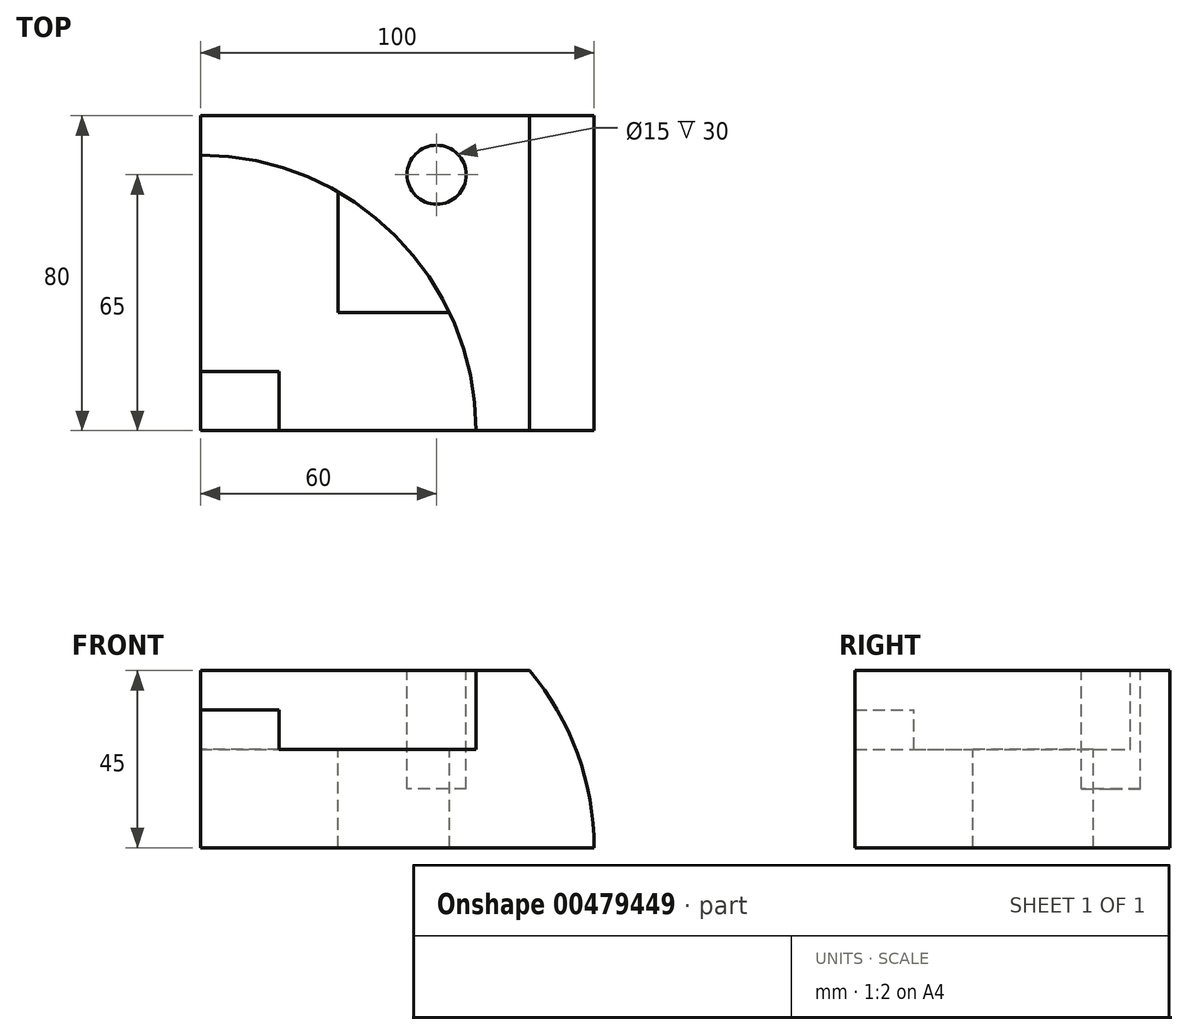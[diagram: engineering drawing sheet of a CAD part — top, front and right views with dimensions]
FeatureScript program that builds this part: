
annotation { "Feature Type Name" : "Feature", "Feature Type Description" : "" }
export const myFeature = defineFeature(function(context is Context, id is Id, definition is map)
    precondition{}
    {
        {
            var Q0;
            Q0=qCreatedBy(makeId("Top.planeOp"),FACE);
            var sketch = newSketch(context, id + "F0", { "sketchPlane" : qUnion([Q0])});
            skLineSegment(sketch, "E0.bottom", {"start": v(0, 0) * mm, "end": v(100, 0) * mm});
            skLineSegment(sketch, "E0.top", {"start": v(0, 80) * mm, "end": v(100, 80) * mm});
            skLineSegment(sketch, "E0.left", {"start": v(0, 0) * mm, "end": v(0, 80) * mm});
            skLineSegment(sketch, "E0.right", {"start": v(100, 0) * mm, "end": v(100, 80) * mm});
            skSolve(sketch);
        }
        {
            var Q0;
            Q0 = qSketchRegion(id + "F0", true);
            extrude(context, id + "F1", {"entities" : qUnion([Q0]), "depth" : 45 * mm});
        }
        {
            var Q0;
            Q0=makeQuery(id+"F1.opExtrude","SWEPT_FACE",FACE,{"disambiguationData":[OSD([sQuery(id+"F0.wireOp",EDGE,"E0.bottom")])]});
            var sketch = newSketch(context, id + "F2", { "sketchPlane" : qUnion([Q0])});
            skLineSegment(sketch, "E1", {"start": v(100, 45) * mm, "end": v(100, 0) * mm});
            skArc(sketch, "E2", {"start": v(100, 0) * mm, "mid": v(95.78, 23.94) * mm, "end": v(83.62, 45) * mm});
            skLineSegment(sketch, "E3", {"start": v(83.62, 45) * mm, "end": v(100, 45) * mm});
            skSolve(sketch);
        }
        {
            var Q0;
            Q0=makeQuery(id+"F2.imprint","IMPRINT",FACE,{"disambiguationData":[TD([[makeQuery(id+"F2.imprint","IMPRINT",EDGE,{"derivedFrom":sQuery(id+"F2.wireOp",EDGE,"E1")}),-1.0]])]});
            extrude(context, id + "F3", {"entities" : qUnion([Q0]), "operationType" : NewBodyOperationType.REMOVE, "endBound" : BoundingType.THROUGH_ALL, "oppositeDirection" : true, "depth" : 25 * mm});
        }
        {
            var Q0;
            Q0=makeQuery(id+"F1.opExtrude","CAP_FACE",FACE,{"disambiguationData":[OSD([sQuery(id+"F0.wireOp",EDGE,"E0.bottom"),sQuery(id+"F0.wireOp",EDGE,"E0.top"),sQuery(id+"F0.wireOp",EDGE,"E0.left"),sQuery(id+"F0.wireOp",EDGE,"E0.right")])],"isStart":false});
            var sketch = newSketch(context, id + "F4", { "sketchPlane" : qUnion([Q0])});
            skArc(sketch, "E4", {"start": v(70, 0) * mm, "mid": v(49.5, 49.5) * mm, "end": v(0, 70) * mm});
            skLineSegment(sketch, "E5.bottom", {"start": v(0, 0) * mm, "end": v(20, 0) * mm});
            skLineSegment(sketch, "E5.top", {"start": v(0, 15) * mm, "end": v(20, 15) * mm});
            skLineSegment(sketch, "E5.left", {"start": v(0, 0) * mm, "end": v(0, 15) * mm});
            skLineSegment(sketch, "E5.right", {"start": v(20, 0) * mm, "end": v(20, 15) * mm});
            skSolve(sketch);
        }
        {
            var Q0;
            {var subQ0=sQuery(id+"F4.wireOp",EDGE,"E4");Q0=makeQuery(id+"F4.imprint","IMPRINT",FACE,{"disambiguationData":[TD([[makeQuery(id+"F4.imprint","IMPRINT",EDGE,{"derivedFrom":subQ0}),1.0]])]});}
            extrude(context, id + "F5", {"entities" : qUnion([Q0]), "operationType" : NewBodyOperationType.REMOVE, "oppositeDirection" : true, "depth" : 20 * mm});
        }
        {
            var Q0;
            {var subQ0=sQuery(id+"F0.wireOp",EDGE,"E0.bottom");var subQ1=sQuery(id+"F0.wireOp",EDGE,"E0.left");Q0=makeQuery(id+"F5.boolean.opBoolean","SPLIT",FACE,{"disambiguationData":[TD([makeQuery(id+"F5.opExtrude","SWEPT_FACE",FACE,{"disambiguationData":[OSD([sQuery(id+"F4.wireOp",EDGE,"E5.top")])]})])],"derivedFrom":makeQuery(id+"F1.opExtrude","CAP_FACE",FACE,{"disambiguationData":[OSD([subQ0,sQuery(id+"F0.wireOp",EDGE,"E0.top"),subQ1,sQuery(id+"F0.wireOp",EDGE,"E0.right")])],"isStart":false})});}
            extrude(context, id + "F6", {"entities" : qUnion([Q0]), "operationType" : NewBodyOperationType.REMOVE, "oppositeDirection" : true, "depth" : 10 * mm});
        }
        {
            var Q0;
            {var subQ0=sQuery(id+"F0.wireOp",EDGE,"E0.left");var subQ1=sQuery(id+"F0.wireOp",EDGE,"E0.top");var subQ2=sQuery(id+"F0.wireOp",EDGE,"E0.bottom");Q0=makeQuery(id+"F5.boolean.opBoolean","SPLIT",FACE,{"disambiguationData":[TD([makeQuery(id+"F1.opExtrude","SWEPT_FACE",FACE,{"disambiguationData":[OSD([subQ1])]})])],"derivedFrom":makeQuery(id+"F1.opExtrude","CAP_FACE",FACE,{"disambiguationData":[OSD([subQ2,subQ1,subQ0,sQuery(id+"F0.wireOp",EDGE,"E0.right")])],"isStart":false})});}
            var sketch = newSketch(context, id + "F7", { "sketchPlane" : qUnion([Q0])});
            skCircle(sketch, "E6", {"center": v(60, 65) * mm, "radius": 7.5 * mm});
            skSolve(sketch);
        }
        {
            var Q0;
            Q0 = qSketchRegion(id + "F7", true);
            extrude(context, id + "F8", {"entities" : qUnion([Q0]), "operationType" : NewBodyOperationType.REMOVE, "oppositeDirection" : true, "depth" : 30 * mm});
        }
        {
            var Q0;
            Q0=makeQuery(id+"F5.boolean.opBoolean","COPY",FACE,{"derivedFrom":makeQuery(id+"F5.opExtrude","CAP_FACE",FACE,{"disambiguationData":[OSD([sQuery(id+"F0.wireOp",EDGE,"E0.bottom"),sQuery(id+"F0.wireOp",EDGE,"E0.left"),sQuery(id+"F4.wireOp",EDGE,"E4"),sQuery(id+"F4.wireOp",EDGE,"E5.top"),sQuery(id+"F4.wireOp",EDGE,"E5.right")])],"isStart":false})});
            var sketch = newSketch(context, id + "F9", { "sketchPlane" : qUnion([Q0])});
            skLineSegment(sketch, "E7", {"start": v(35, 60.62) * mm, "end": v(35, 30) * mm});
            skLineSegment(sketch, "E8", {"start": v(35, 30) * mm, "end": v(63.25, 30) * mm});
            skSolve(sketch);
        }
        {
            var Q0;
            {var subQ0=sQuery(id+"F9.wireOp",EDGE,"E7");Q0=makeQuery(id+"F9.imprint","IMPRINT",FACE,{"disambiguationData":[TD([[makeQuery(id+"F9.imprint","IMPRINT",EDGE,{"derivedFrom":subQ0}),1.0]])]});}
            extrude(context, id + "F10", {"entities" : qUnion([Q0]), "operationType" : NewBodyOperationType.REMOVE, "endBound" : BoundingType.THROUGH_ALL, "oppositeDirection" : true, "depth" : 25 * mm});
        }
    });
